# Revit family: P6480-THTD
name_source: partatom
category: Plumbing Fixtures
revit_build: Autodesk Revit 2018 (Build: 20170223_1515(x64)
units: mm (PartAtom-declared; Revit-internal decimal feet)

## family parameters
Cut with Voids When Loaded = No
Host = Face
Part Type = Normal
Room Calculation Point = No
Round Connector Dimension = Use Diameter
Shared = No

## types (6) — shared parameters
Default Elevation = 4' - 0"
Description = 8" WIDE, STAINLESS STEEL THRESHOLD DRAIN
Manufacturer = MIFAB
Material = Paint - Sherwin Williams Paint - #952C2A - Bellwood Red
Radius = 0' - 2"
URL = WWW.MIFAB.COM

## per-type parameters (varying)
| type | Clamp space | Diameter | First position | Length | Number of Clamp |
| P6480-THTD-36 | 0' - 9" | 0' - 3 7/8" | 0' - 4 1/2" | 3' - 0" | 4 |
| P6480-THTD-48 | 1' - 0" | 0' - 4" | 0' - 6" | 4' - 0" | 4 |
| P6480-THTD-96 | 1' - 7 3/16" | 0' - 4" | 0' - 9 5/8" | 8' - 0" | 5 |
| P6480-THTD-108 | 1' - 9 5/8" | 0' - 4" | 0' - 10 13/16" | 9' - 0" | 5 |
| P6480-THTD-60 | 1' - 3" | 0' - 3 7/8" | 0' - 7 1/2" | 5' - 0" | 4 |
| P6480-THTD-72 | 1' - 7 3/16" | 0' - 3 7/8" | 0' - 4 13/16" | 6' - 0" | 4 |

note: column(s) folded — value = type name in every type: Model

## geometry (parser evidence)
native form markers: Sweep x5
no freeform markers — native parametric forms only
